# Revit family: Lighting-Recessed-Ledalite-TruGroove-LED_Flat_Corner V
name_source: partatom
category: Lighting Fixtures
revit_build: Autodesk Revit 2017 (Build: 20160720_1515(x64)
units: mm (PartAtom-declared; Revit-internal decimal feet)

## family parameters
Cut with Voids When Loaded = No
Host = Face
Light Source = Yes
OmniClass Number = 23.80.70.11.14
OmniClass Title = General Luminaries, Directional
Part Type = Normal
Room Calculation Point = No
Round Connector Dimension = Use Diameter
Shared = No

## types (135) — shared parameters
Assembly Code = D5020200
CIE Type = Direct
Color Filter = 16777215
Default Elevation = 48"
Dimming Lamp Color Temperature Shift = <None>
Fixture Efficiency = NA (Absolute Photometry)
Housing Length = 25 11/16"
Housing Material Finish = Paint-Signify-White
Housing Width = 3 7/16"
Lamp = LED
Last Updated = 11/6/2014
Lens Material Finish = Acrylic-Signify-White, Translucent
Lens Width = 3"
Manufacturer = Ledalite
NEMA Type = Not Applicable
Photometry Comments = Candela values are absolute.
Product Family = TruGroove
Product Page URL = http://www.lightingproducts.philips.com
Tilt Angle = -90.00°
URL = https://www.signify.com
Voltage = 120 V
eCatalog URL = www.ledalite.com

## per-type parameters (varying)
| type | Apparent Load | Depth | Depth below Ceiling | Description | LER Luminaire Efficacy Rating | Photometric Web File | Spacing to Mounting Height Ratio 0 Degree Plane | Spacing to Mounting Height Ratio 90 Degree Plane | Spacing to Mounting Height Ratio Diagonal | Trim | Trim Length | Trim Width | Trimless/TGrid |
| 39A0LAELx122 | 42 VA | 4 23/32" | 0" | 2x2 Flat Corner, Definition LED, 4000K, 3000 Nominal Delivered Lumens, Flush Silk Lens, T-Grid | 72 | 39x0LAELxx04.ies | 1.28 | 1.28 | 1.4 | No | 25 29/32" | 4" | Yes |
| 39A0LAELx422 | 42 VA | 4 7/8" | 5/32" | 2x2 Flat Corner, Definition LED, 4000K, 3000 Nominal Delivered Lumens, Flush Silk Lens, Drywall Trim | 72 | 39x0LAELxx04.ies | 1.28 | 1.28 | 1.4 | Yes | 26 5/16" | 4 1/2" | No |
| 39A0LAELx322 | 42 VA | 4 7/8" | 5/32" | 2x2 Flat Corner, Definition LED, 4000K, 3000 Nominal Delivered Lumens, Flush Silk Lens, Drywall Trimless | 72 | 39x0LAELxx04.ies | 1.28 | 1.28 | 1.4 | No | 27 3/32" | 6 1/4" | Yes |
| 39A0LAEMx122 | 42 VA | 4 23/32" | 0" | 2x2 Flat Corner, Definition LED, 4000K, 3000 Nominal Delivered Lumens, Regressed Silk Lens, T-Grid | 60 | 39x0LAEMxx04.ies | 1.28 | 1.24 | 1.36 | No | 25 29/32" | 4" | Yes |
| 39A0LAEMx422 | 42 VA | 4 7/8" | 5/32" | 2x2 Flat Corner, Definition LED, 4000K, 3000 Nominal Delivered Lumens, Regressed Silk Lens, Drywall Trim | 60 | 39x0LAEMxx04.ies | 1.28 | 1.24 | 1.36 | Yes | 26 5/16" | 4 1/2" | No |
| 39A0LAEMx322 | 42 VA | 4 7/8" | 5/32" | 2x2 Flat Corner, Definition LED, 4000K, 3000 Nominal Delivered Lumens, Regressed Silk Lens, Drywall Trimless | 60 | 39x0LAEMxx04.ies | 1.28 | 1.24 | 1.36 | No | 27 3/32" | 6 1/4" | Yes |
| 39A0LAGLx122 | 28 VA | 4 23/32" | 0" | 2x2 Flat Corner, Definition LED, 4000K, 2200 Nominal Delivered Lumens, Flush Silk Lens, T-Grid | 77 | 39x0LAGLxx04.ies | 1.28 | 1.28 | 1.4 | No | 25 29/32" | 4" | Yes |
| 39A0LAGLx422 | 28 VA | 4 7/8" | 5/32" | 2x2 Flat Corner, Definition LED, 4000K, 2200 Nominal Delivered Lumens, Flush Silk Lens, Drywall Trim | 77 | 39x0LAGLxx04.ies | 1.28 | 1.28 | 1.4 | Yes | 26 5/16" | 4 1/2" | No |
| 39A0LAGLx322 | 28 VA | 4 7/8" | 5/32" | 2x2 Flat Corner, Definition LED, 4000K, 2200 Nominal Delivered Lumens, Flush Silk Lens, Drywall Trimless | 77 | 39x0LAGLxx04.ies | 1.28 | 1.28 | 1.4 | No | 27 3/32" | 6 1/4" | Yes |
| 39A0LAGMx122 | 28 VA | 4 23/32" | 0" | 2x2 Flat Corner, Definition LED, 4000K, 2200 Nominal Delivered Lumens, Regressed Silk Lens, T-Grid | 64 | 39x0LAGMxx04.ies | 1.28 | 1.24 | 1.36 | No | 25 29/32" | 4" | Yes |
| 39A0LAGMx422 | 28 VA | 4 7/8" | 5/32" | 2x2 Flat Corner, Definition LED, 4000K, 2200 Nominal Delivered Lumens, Regressed Silk Lens, Drywall Trim | 64 | 39x0LAGMxx04.ies | 1.28 | 1.24 | 1.36 | Yes | 26 5/16" | 4 1/2" | No |
| 39A0LAGMx322 | 28 VA | 4 7/8" | 5/32" | 2x2 Flat Corner, Definition LED, 4000K, 2200 Nominal Delivered Lumens, Regressed Silk Lens, Drywall Trimless | 64 | 39x0LAGMxx04.ies | 1.28 | 1.24 | 1.36 | No | 27 3/32" | 6 1/4" | Yes |
| 39A0LAKLx122 | 19 VA | 4 23/32" | 0" | 2x2 Flat Corner, Definition LED, 4000K, 1500 Nominal Delivered Lumens, Flush Silk Lens, T-Grid | 80 | 39x0LAKLxx04.ies | 1.28 | 1.28 | 1.4 | No | 25 29/32" | 4" | Yes |
| 39A0LAKLx422 | 19 VA | 4 7/8" | 5/32" | 2x2 Flat Corner, Definition LED, 4000K, 1500 Nominal Delivered Lumens, Flush Silk Lens, Drywall Trim | 80 | 39x0LAKLxx04.ies | 1.28 | 1.28 | 1.4 | Yes | 26 5/16" | 4 1/2" | No |
| 39A0LAKLx322 | 19 VA | 4 7/8" | 5/32" | 2x2 Flat Corner, Definition LED, 4000K, 1500 Nominal Delivered Lumens, Flush Silk Lens, Drywall Trimless | 80 | 39x0LAKLxx04.ies | 1.28 | 1.28 | 1.4 | No | 27 3/32" | 6 1/4" | Yes |
| 39A0LAKMx122 | 19 VA | 4 23/32" | 0" | 2x2 Flat Corner, Definition LED, 4000K, 1500 Nominal Delivered Lumens, Regressed Silk Lens, T-Grid | 66 | 39x0LAKMxx04.ies | 1.28 | 1.24 | 1.36 | No | 25 29/32" | 4" | Yes |
| 39A0LAKMx422 | 19 VA | 4 7/8" | 5/32" | 2x2 Flat Corner, Definition LED, 4000K, 1500 Nominal Delivered Lumens, Regressed Silk Lens, Drywall Trim | 66 | 39x0LAKMxx04.ies | 1.28 | 1.24 | 1.36 | Yes | 26 5/16" | 4 1/2" | No |
| 39A0LAKMx322 | 19 VA | 4 7/8" | 5/32" | 2x2 Flat Corner, Definition LED, 4000K, 1500 Nominal Delivered Lumens, Regressed Silk Lens, Drywall Trimless | 66 | 39x0LAKMxx04.ies | 1.28 | 1.24 | 1.36 | No | 27 3/32" | 6 1/4" | Yes |
| 39A0LBELx122 | 41 VA | 4 23/32" | 0" | 2x2 Flat Corner, Definition LED, 3500K, 3000 Nominal Delivered Lumens, Flush Silk Lens, T-Grid | 73 | 39x0LBELxx04.ies | 1.28 | 1.28 | 1.4 | No | 25 29/32" | 4" | Yes |
| 39A0LBELx422 | 41 VA | 4 7/8" | 5/32" | 2x2 Flat Corner, Definition LED, 3500K, 3000 Nominal Delivered Lumens, Flush Silk Lens, Drywall Trim | 73 | 39x0LBELxx04.ies | 1.28 | 1.28 | 1.4 | Yes | 26 5/16" | 4 1/2" | No |
| 39A0LBELx322 | 41 VA | 4 7/8" | 5/32" | 2x2 Flat Corner, Definition LED, 3500K, 3000 Nominal Delivered Lumens, Flush Silk Lens, Drywall Trimless | 73 | 39x0LBELxx04.ies | 1.28 | 1.28 | 1.4 | No | 27 3/32" | 6 1/4" | Yes |
| 39A0LBEMx122 | 42 VA | 4 23/32" | 0" | 2x2 Flat Corner, Definition LED, 3500K, 3000 Nominal Delivered Lumens, Regressed Silk Lens, T-Grid | 61 | 39x0LBEMxx04.ies | 1.28 | 1.24 | 1.36 | No | 25 29/32" | 4" | Yes |
| 39A0LBEMx422 | 42 VA | 4 7/8" | 5/32" | 2x2 Flat Corner, Definition LED, 3500K, 3000 Nominal Delivered Lumens, Regressed Silk Lens, Drywall Trim | 61 | 39x0LBEMxx04.ies | 1.28 | 1.24 | 1.36 | Yes | 26 5/16" | 4 1/2" | No |
| 39A0LBEMx322 | 42 VA | 4 7/8" | 5/32" | 2x2 Flat Corner, Definition LED, 3500K, 3000 Nominal Delivered Lumens, Regressed Silk Lens, Drywall Trimless | 61 | 39x0LBEMxx04.ies | 1.28 | 1.24 | 1.36 | No | 27 3/32" | 6 1/4" | Yes |
| 39A0LBGLx122 | 28 VA | 4 23/32" | 0" | 2x2 Flat Corner, Definition LED, 3500K, 2200 Nominal Delivered Lumens, Flush Silk Lens, T-Grid | 78 | 39x0LBGLxx04.ies | 1.28 | 1.28 | 1.4 | No | 25 29/32" | 4" | Yes |
| 39A0LBGLx422 | 28 VA | 4 7/8" | 5/32" | 2x2 Flat Corner, Definition LED, 3500K, 2200 Nominal Delivered Lumens, Flush Silk Lens, Drywall Trim | 78 | 39x0LBGLxx04.ies | 1.28 | 1.28 | 1.4 | Yes | 26 5/16" | 4 1/2" | No |
| 39A0LBGLx322 | 28 VA | 4 7/8" | 5/32" | 2x2 Flat Corner, Definition LED, 3500K, 2200 Nominal Delivered Lumens, Flush Silk Lens, Drywall Trimless | 78 | 39x0LBGLxx04.ies | 1.28 | 1.28 | 1.4 | No | 27 3/32" | 6 1/4" | Yes |
| 39A0LBGMx122 | 28 VA | 4 23/32" | 0" | 2x2 Flat Corner, Definition LED, 3500K, 2200 Nominal Delivered Lumens, Regressed Silk Lens, T-Grid | 66 | 39x0LBGMxx04.ies | 1.28 | 1.24 | 1.36 | No | 25 29/32" | 4" | Yes |
| 39A0LBGMx422 | 28 VA | 4 7/8" | 5/32" | 2x2 Flat Corner, Definition LED, 3500K, 2200 Nominal Delivered Lumens, Regressed Silk Lens, Drywall Trim | 66 | 39x0LBGMxx04.ies | 1.28 | 1.24 | 1.36 | Yes | 26 5/16" | 4 1/2" | No |
| 39A0LBGMx322 | 28 VA | 4 7/8" | 5/32" | 2x2 Flat Corner, Definition LED, 3500K, 2200 Nominal Delivered Lumens, Regressed Silk Lens, Drywall Trimless | 66 | 39x0LBGMxx04.ies | 1.28 | 1.24 | 1.36 | No | 27 3/32" | 6 1/4" | Yes |
| 39A0LBKLx122 | 19 VA | 4 23/32" | 0" | 2x2 Flat Corner, Definition LED, 3500K, 1500 Nominal Delivered Lumens, Flush Silk Lens, T-Grid | 81 | 39x0LBKLxx04.ies | 1.28 | 1.28 | 1.4 | No | 25 29/32" | 4" | Yes |
| 39A0LBKLx422 | 19 VA | 4 7/8" | 5/32" | 2x2 Flat Corner, Definition LED, 3500K, 1500 Nominal Delivered Lumens, Flush Silk Lens, Drywall Trim | 81 | 39x0LBKLxx04.ies | 1.28 | 1.28 | 1.4 | Yes | 26 5/16" | 4 1/2" | No |
| 39A0LBKLx322 | 19 VA | 4 7/8" | 5/32" | 2x2 Flat Corner, Definition LED, 3500K, 1500 Nominal Delivered Lumens, Flush Silk Lens, Drywall Trimless | 81 | 39x0LBKLxx04.ies | 1.28 | 1.28 | 1.4 | No | 27 3/32" | 6 1/4" | Yes |
| 39A0LBKMx122 | 19 VA | 4 23/32" | 0" | 2x2 Flat Corner, Definition LED, 3500K, 1500 Nominal Delivered Lumens, Regressed Silk Lens, T-Grid | 67 | 39x0LBKMxx04.ies | 1.28 | 1.24 | 1.36 | No | 25 29/32" | 4" | Yes |
| 39A0LBKMx422 | 19 VA | 4 7/8" | 5/32" | 2x2 Flat Corner, Definition LED, 3500K, 1500 Nominal Delivered Lumens, Regressed Silk Lens, Drywall Trim | 67 | 39x0LBKMxx04.ies | 1.28 | 1.24 | 1.36 | Yes | 26 5/16" | 4 1/2" | No |
| 39A0LBKMx322 | 0 VA | 4 7/8" | 5/32" | 2x2 Flat Corner, Definition LED, 3500K, 1500 Nominal Delivered Lumens, Regressed Silk Lens, Drywall Trimless | 67 | 39x0LBKMxx04.ies | 1.28 | 1.24 | 1.36 | No | 27 3/32" | 6 1/4" | Yes |
| 39A0LCELx122 | 42 VA | 4 23/32" | 0" | 2x2 Flat Corner, Definition LED, 3000K, 3000 Nominal Delivered Lumens, Flush Silk Lens, T-Grid | 70 | 39x0LCELxx04.ies | 1.28 | 1.28 | 1.4 | No | 25 29/32" | 4" | Yes |
| 39A0LCELx422 | 42 VA | 4 7/8" | 5/32" | 2x2 Flat Corner, Definition LED, 3000K, 3000 Nominal Delivered Lumens, Flush Silk Lens, Drywall Trim | 70 | 39x0LCELxx04.ies | 1.28 | 1.28 | 1.4 | Yes | 26 5/16" | 4 1/2" | No |
| 39A0LCELx322 | 42 VA | 4 7/8" | 5/32" | 2x2 Flat Corner, Definition LED, 3000K, 3000 Nominal Delivered Lumens, Flush Silk Lens, Drywall Trimless | 70 | 39x0LCELxx04.ies | 1.28 | 1.28 | 1.4 | No | 27 3/32" | 6 1/4" | Yes |
| 39A0LCEMx122 | 42 VA | 4 23/32" | 0" | 2x2 Flat Corner, Definition LED, 3000K, 3000 Nominal Delivered Lumens, Regressed Silk Lens, T-Grid | 58 | 39x0LCEMxx04.ies | 1.28 | 1.24 | 1.36 | No | 25 29/32" | 4" | Yes |
| 39A0LCEMx422 | 42 VA | 4 7/8" | 5/32" | 2x2 Flat Corner, Definition LED, 3000K, 3000 Nominal Delivered Lumens, Regressed Silk Lens, Drywall Trim | 58 | 39x0LCEMxx04.ies | 1.28 | 1.24 | 1.36 | Yes | 26 5/16" | 4 1/2" | No |
| 39A0LCEMx322 | 42 VA | 4 7/8" | 5/32" | 2x2 Flat Corner, Definition LED, 3000K, 3000 Nominal Delivered Lumens, Regressed Silk Lens, Drywall Trimless | 58 | 39x0LCEMxx04.ies | 1.28 | 1.24 | 1.36 | No | 27 3/32" | 6 1/4" | Yes |
| 39A0LCGLx122 | 28 VA | 4 23/32" | 0" | 2x2 Flat Corner, Definition LED, 3000K, 2200 Nominal Delivered Lumens, Flush Silk Lens, T-Grid | 75 | 39x0LCGLxx04.ies | 1.28 | 1.28 | 1.4 | No | 25 29/32" | 4" | Yes |
| 39A0LCGLx422 | 28 VA | 4 7/8" | 5/32" | 2x2 Flat Corner, Definition LED, 3000K, 2200 Nominal Delivered Lumens, Flush Silk Lens, Drywall Trim | 75 | 39x0LCGLxx04.ies | 1.28 | 1.28 | 1.4 | Yes | 26 5/16" | 4 1/2" | No |
| 39A0LCGLx322 | 28 VA | 4 7/8" | 5/32" | 2x2 Flat Corner, Definition LED, 3000K, 2200 Nominal Delivered Lumens, Flush Silk Lens, Drywall Trimless | 75 | 39x0LCGLxx04.ies | 1.28 | 1.28 | 1.4 | No | 27 3/32" | 6 1/4" | Yes |
| 39A0LCGMx122 | 28 VA | 4 23/32" | 0" | 2x2 Flat Corner, Definition LED, 3000K, 2200 Nominal Delivered Lumens, Regressed Silk Lens, T-Grid | 62 | 39x0LCGMxx04.ies | 1.28 | 1.24 | 1.36 | No | 25 29/32" | 4" | Yes |
| 39A0LCGMx422 | 28 VA | 4 7/8" | 5/32" | 2x2 Flat Corner, Definition LED, 3000K, 2200 Nominal Delivered Lumens, Regressed Silk Lens, Drywall Trim | 62 | 39x0LCGMxx04.ies | 1.28 | 1.24 | 1.36 | Yes | 26 5/16" | 4 1/2" | No |
| 39A0LCGMx322 | 28 VA | 4 7/8" | 5/32" | 2x2 Flat Corner, Definition LED, 3000K, 2200 Nominal Delivered Lumens, Regressed Silk Lens, Drywall Trimless | 62 | 39x0LCGMxx04.ies | 1.28 | 1.24 | 1.36 | No | 27 3/32" | 6 1/4" | Yes |
| 39A0LCKLx122 | 19 VA | 4 23/32" | 0" | 2x2 Flat Corner, Definition LED, 3000K, 1500 Nominal Delivered Lumens, Flush Silk Lens, T-Grid | 77 | 39x0LCKLxx04.ies | 1.28 | 1.28 | 1.4 | No | 25 29/32" | 4" | Yes |
| 39A0LCKLx422 | 19 VA | 4 7/8" | 5/32" | 2x2 Flat Corner, Definition LED, 3000K, 1500 Nominal Delivered Lumens, Flush Silk Lens, Drywall Trim | 77 | 39x0LCKLxx04.ies | 1.28 | 1.28 | 1.4 | Yes | 26 5/16" | 4 1/2" | No |
| 39A0LCKLx322 | 19 VA | 4 7/8" | 5/32" | 2x2 Flat Corner, Definition LED, 3000K, 1500 Nominal Delivered Lumens, Flush Silk Lens, Drywall Trimless | 77 | 39x0LCKLxx04.ies | 1.28 | 1.28 | 1.4 | No | 27 3/32" | 6 1/4" | Yes |
| 39A0LCKMx122 | 19 VA | 4 23/32" | 0" | 2x2 Flat Corner, Definition LED, 3000K, 1500 Nominal Delivered Lumens, Regressed Silk Lens, T-Grid | 65 | 39x0LCKMxx04.ies | 1.28 | 1.24 | 1.36 | No | 25 29/32" | 4" | Yes |
| 39A0LCKMx422 | 19 VA | 4 7/8" | 5/32" | 2x2 Flat Corner, Definition LED, 3000K, 1500 Nominal Delivered Lumens, Regressed Silk Lens, Drywall Trim | 65 | 39x0LCKMxx04.ies | 1.28 | 1.24 | 1.36 | Yes | 26 5/16" | 4 1/2" | No |
| 39A0LCKMx322 | 19 VA | 4 7/8" | 5/32" | 2x2 Flat Corner, Definition LED, 3000K, 1500 Nominal Delivered Lumens, Regressed Silk Lens, Drywall Trimless | 65 | 39x0LCKMxx04.ies | 1.28 | 1.24 | 1.36 | No | 27 3/32" | 6 1/4" | Yes |
| 39A1LAEQx122 | 42 VA | 4 23/32" | 0" | 2x2 Flat Corner, Performance LED, 4000K, 3000 Nominal Delivered Lumens, Flush Meso Lens, T- Grid | 73 | 39x1LAEQxx04.ies | 1.42 | 1.76 | 1.52 | No | 25 29/32" | 4" | Yes |
| 39A1LAEQx422 | 42 VA | 4 7/8" | 5/32" | 2x2 Flat Corner, Performance LED, 4000K, 3000 Nominal Delivered Lumens, Flush Meso Lens, Drywall Trim | 73 | 39x1LAEQxx04.ies | 1.42 | 1.76 | 1.52 | Yes | 26 5/16" | 4 1/2" | No |
| 39A1LAEQx322 | 42 VA | 4 7/8" | 5/32" | 2x2 Flat Corner, Performance LED, 4000K, 3000 Nominal Delivered Lumens, Flush Meso Lens, Drywall Trimless | 73 | 39x1LAEQxx04.ies | 1.42 | 1.76 | 1.52 | No | 27 3/32" | 6 1/4" | Yes |
| 39A1LAERx122 | 42 VA | 4 23/32" | 0" | 2x2 Flat Corner, Performance LED, 4000K, 3000 Nominal Delivered Lumens, Regressed Meso Lens, T- Grid | 64 | 39x1LAERxx04.ies | 1.34 | 1.5 | 1.4 | No | 25 29/32" | 4" | Yes |
| 39A1LAERx422 | 42 VA | 4 7/8" | 5/32" | 2x2 Flat Corner, Performance LED, 4000K, 3000 Nominal Delivered Lumens, Regressed Meso Lens, Drywall Trim | 64 | 39x1LAERxx04.ies | 1.34 | 1.5 | 1.4 | Yes | 26 5/16" | 4 1/2" | No |
| 39A1LAERx322 | 42 VA | 4 7/8" | 5/32" | 2x2 Flat Corner, Performance LED, 4000K, 3000 Nominal Delivered Lumens, Regressed Meso Lens, Drywall Trimless | 64 | 39x1LAERxx04.ies | 1.34 | 1.5 | 1.4 | No | 27 3/32" | 6 1/4" | Yes |
| 39A1LAGQx122 | 28 VA | 4 23/32" | 0" | 2x2 Flat Corner, Performance LED, 4000K, 2200 Nominal Delivered Lumens, Flush Meso Lens, T- Grid | 78 | 39x1LAGQxx04.ies | 1.42 | 1.76 | 1.52 | No | 25 29/32" | 4" | Yes |
| 39A1LAGQx422 | 28 VA | 4 7/8" | 5/32" | 2x2 Flat Corner, Performance LED, 4000K, 2200 Nominal Delivered Lumens, Flush Meso Lens, Drywall Trim | 78 | 39x1LAGQxx04.ies | 1.42 | 1.76 | 1.52 | Yes | 26 5/16" | 4 1/2" | No |
| 39A1LAGQx322 | 28 VA | 4 7/8" | 5/32" | 2x2 Flat Corner, Performance LED, 4000K, 2200 Nominal Delivered Lumens, Flush Meso Lens, Drywall Trimless | 78 | 39x1LAGQxx04.ies | 1.42 | 1.76 | 1.52 | No | 27 3/32" | 6 1/4" | Yes |
| 39A1LAGRx122 | 28 VA | 4 23/32" | 0" | 2x2 Flat Corner, Performance LED, 4000K, 2200 Nominal Delivered Lumens, Regressed Meso Lens, T- Grid | 69 | 39x1LAGRxx04.ies | 1.34 | 1.5 | 1.4 | No | 25 29/32" | 4" | Yes |
| 39A1LAGRx422 | 28 VA | 4 7/8" | 5/32" | 2x2 Flat Corner, Performance LED, 4000K, 2200 Nominal Delivered Lumens, Regressed Meso Lens, Drywall Trim | 69 | 39x1LAGRxx04.ies | 1.34 | 1.5 | 1.4 | Yes | 26 5/16" | 4 1/2" | No |
| 39A1LAGRx322 | 28 VA | 4 7/8" | 5/32" | 2x2 Flat Corner, Performance LED, 4000K, 2200 Nominal Delivered Lumens, Regressed Meso Lens, Drywall Trimless | 69 | 39x1LAGRxx04.ies | 1.34 | 1.5 | 1.4 | No | 27 3/32" | 6 1/4" | Yes |
| 39A1LAKQx122 | 19 VA | 4 23/32" | 0" | 2x2 Flat Corner, Performance LED, 4000K, 1500 Nominal Delivered Lumens, Flush Meso Lens, T- Grid | 81 | 39x1LAKQxx04.ies | 1.42 | 1.76 | 1.52 | No | 25 29/32" | 4" | Yes |
| 39A1LAKQx422 | 19 VA | 4 7/8" | 5/32" | 2x2 Flat Corner, Performance LED, 4000K, 1500 Nominal Delivered Lumens, Flush Meso Lens, Drywall Trim | 81 | 39x1LAKQxx04.ies | 1.42 | 1.76 | 1.52 | Yes | 26 5/16" | 4 1/2" | No |
| 39A1LAKQx322 | 19 VA | 4 7/8" | 5/32" | 2x2 Flat Corner, Performance LED, 4000K, 1500 Nominal Delivered Lumens, Flush Meso Lens, Drywall Trimless | 81 | 39x1LAKQxx04.ies | 1.42 | 1.76 | 1.52 | No | 27 3/32" | 6 1/4" | Yes |
| 39A1LAKRx122 | 19 VA | 4 23/32" | 0" | 2x2 Flat Corner, Performance LED, 4000K, 1500 Nominal Delivered Lumens, Regressed Meso Lens, T- Grid | 71 | 39x1LAKRxx04.ies | 1.34 | 1.5 | 1.4 | No | 25 29/32" | 4" | Yes |
| 39A1LAKRx422 | 19 VA | 4 7/8" | 5/32" | 2x2 Flat Corner, Performance LED, 4000K, 1500 Nominal Delivered Lumens, Regressed Meso Lens, Drywall Trim | 71 | 39x1LAKRxx04.ies | 1.34 | 1.5 | 1.4 | Yes | 26 5/16" | 4 1/2" | No |
| 39A1LAKRx322 | 19 VA | 4 7/8" | 5/32" | 2x2 Flat Corner, Performance LED, 4000K, 1500 Nominal Delivered Lumens, Regressed Meso Lens, Drywall Trimless | 71 | 39x1LAKRxx04.ies | 1.34 | 1.5 | 1.4 | No | 27 3/32" | 6 1/4" | Yes |
| 39A1LBEQx122 | 41 VA | 4 23/32" | 0" | 2x2 Flat Corner, Performance LED, 3500K, 3000 Nominal Delivered Lumens, Flush Meso Lens, T- Grid | 74 | 39x1LBEQxx04.ies | 1.42 | 1.76 | 1.52 | No | 25 29/32" | 4" | Yes |
| 39A1LBEQx422 | 41 VA | 4 7/8" | 5/32" | 2x2 Flat Corner, Performance LED, 3500K, 3000 Nominal Delivered Lumens, Flush Meso Lens, Drywall Trim | 74 | 39x1LBEQxx04.ies | 1.42 | 1.76 | 1.52 | Yes | 26 5/16" | 4 1/2" | No |
| 39A1LBEQx322 | 41 VA | 4 7/8" | 5/32" | 2x2 Flat Corner, Performance LED, 3500K, 3000 Nominal Delivered Lumens, Flush Meso Lens, Drywall Trimless | 74 | 39x1LBEQxx04.ies | 1.42 | 1.76 | 1.52 | No | 27 3/32" | 6 1/4" | Yes |
| 39A1LBERx122 | 42 VA | 4 23/32" | 0" | 2x2 Flat Corner, Performance LED, 3500K, 3000 Nominal Delivered Lumens, Regressed Meso Lens, T- Grid | 65 | 39x1LBERxx04.ies | 1.34 | 1.5 | 1.4 | No | 25 29/32" | 4" | Yes |
| 39A1LBERx422 | 42 VA | 4 7/8" | 5/32" | 2x2 Flat Corner, Performance LED, 3500K, 3000 Nominal Delivered Lumens, Regressed Meso Lens, Drywall Trim | 65 | 39x1LBERxx04.ies | 1.34 | 1.5 | 1.4 | Yes | 26 5/16" | 4 1/2" | No |
| 39A1LBERx322 | 42 VA | 4 7/8" | 5/32" | 2x2 Flat Corner, Performance LED, 3500K, 3000 Nominal Delivered Lumens, Regressed Meso Lens, Drywall Trimless | 65 | 39x1LBERxx04.ies | 1.34 | 1.5 | 1.4 | No | 27 3/32" | 6 1/4" | Yes |
| 39A1LBGQx122 | 28 VA | 4 23/32" | 0" | 2x2 Flat Corner, Performance LED, 3500K, 2200 Nominal Delivered Lumens, Flush Meso Lens, T- Grid | 80 | 39x1LBGQxx04.ies | 1.42 | 1.76 | 1.52 | No | 25 29/32" | 4" | Yes |
| 39A1LBGQx422 | 28 VA | 4 7/8" | 5/32" | 2x2 Flat Corner, Performance LED, 3500K, 2200 Nominal Delivered Lumens, Flush Meso Lens, Drywall Trim | 80 | 39x1LBGQxx04.ies | 1.42 | 1.76 | 1.52 | Yes | 26 5/16" | 4 1/2" | No |
| 39A1LBGQx322 | 28 VA | 4 7/8" | 5/32" | 2x2 Flat Corner, Performance LED, 3500K, 2200 Nominal Delivered Lumens, Flush Meso Lens, Drywall Trimless | 80 | 39x1LBGQxx04.ies | 1.42 | 1.76 | 1.52 | No | 27 3/32" | 6 1/4" | Yes |
| 39A1LBGRx122 | 28 VA | 4 23/32" | 0" | 2x2 Flat Corner, Performance LED, 3500K, 2200 Nominal Delivered Lumens, Regressed Meso Lens, T- Grid | 70 | 39x1LBGRxx04.ies | 1.34 | 1.5 | 1.4 | No | 25 29/32" | 4" | Yes |
| 39A1LBGRx422 | 28 VA | 4 7/8" | 5/32" | 2x2 Flat Corner, Performance LED, 3500K, 2200 Nominal Delivered Lumens, Regressed Meso Lens, Drywall Trim | 70 | 39x1LBGRxx04.ies | 1.34 | 1.5 | 1.4 | Yes | 26 5/16" | 4 1/2" | No |
| 39A1LBGRx322 | 28 VA | 4 7/8" | 5/32" | 2x2 Flat Corner, Performance LED, 3500K, 2200 Nominal Delivered Lumens, Regressed Meso Lens, Drywall Trimless | 70 | 39x1LBGRxx04.ies | 1.34 | 1.5 | 1.4 | No | 27 3/32" | 6 1/4" | Yes |
| 39A1LBKQx122 | 19 VA | 4 23/32" | 0" | 2x2 Flat Corner, Performance LED, 3500K, 1500 Nominal Delivered Lumens, Flush Meso Lens, T- Grid | 82 | 39x1LBKQxx04.ies | 1.42 | 1.76 | 1.52 | No | 25 29/32" | 4" | Yes |
| 39A1LBKQx422 | 19 VA | 4 7/8" | 5/32" | 2x2 Flat Corner, Performance LED, 3500K, 1500 Nominal Delivered Lumens, Flush Meso Lens, Drywall Trim | 82 | 39x1LBKQxx04.ies | 1.42 | 1.76 | 1.52 | Yes | 26 5/16" | 4 1/2" | No |
| 39A1LBKQx322 | 19 VA | 4 7/8" | 5/32" | 2x2 Flat Corner, Performance LED, 3500K, 1500 Nominal Delivered Lumens, Flush Meso Lens, Drywall Trimless | 82 | 39x1LBKQxx04.ies | 1.42 | 1.76 | 1.52 | No | 27 3/32" | 6 1/4" | Yes |
| 39A1LBKRx122 | 19 VA | 4 23/32" | 0" | 2x2 Flat Corner, Performance LED, 3500K, 1500 Nominal Delivered Lumens, Regressed Meso Lens, T- Grid | 72 | 39x1LBKRxx04.ies | 1.34 | 1.5 | 1.4 | No | 25 29/32" | 4" | Yes |
| 39A1LBKRx422 | 19 VA | 4 7/8" | 5/32" | 2x2 Flat Corner, Performance LED, 3500K, 1500 Nominal Delivered Lumens, Regressed Meso Lens, Drywall Trim | 72 | 39x1LBKRxx04.ies | 1.34 | 1.5 | 1.4 | Yes | 26 5/16" | 4 1/2" | No |
| 39A1LBKRx322 | 19 VA | 4 7/8" | 5/32" | 2x2 Flat Corner, Performance LED, 3500K, 1500 Nominal Delivered Lumens, Regressed Meso Lens, Drywall Trimless | 72 | 39x1LBKRxx04.ies | 1.34 | 1.5 | 1.4 | No | 27 3/32" | 6 1/4" | Yes |
| 39A1LCEQx122 | 42 VA | 4 23/32" | 0" | 2x2 Flat Corner, Performance LED, 3000K, 3000 Nominal Delivered Lumens, Flush Meso Lens, T- Grid | 71 | 39x1LCEQxx04.ies | 1.42 | 1.76 | 1.52 | No | 25 29/32" | 4" | Yes |
| 39A1LCEQx422 | 42 VA | 4 7/8" | 5/32" | 2x2 Flat Corner, Performance LED, 3000K, 3000 Nominal Delivered Lumens, Flush Meso Lens, Drywall Trim | 71 | 39x1LCEQxx04.ies | 1.42 | 1.76 | 1.52 | Yes | 26 5/16" | 4 1/2" | No |
| 39A1LCEQx322 | 42 VA | 4 7/8" | 5/32" | 2x2 Flat Corner, Performance LED, 3000K, 3000 Nominal Delivered Lumens, Flush Meso Lens, Drywall Trimless | 71 | 39x1LCEQxx04.ies | 1.42 | 1.76 | 1.52 | No | 27 3/32" | 6 1/4" | Yes |
| 39A1LCERx122 | 42 VA | 4 23/32" | 0" | 2x2 Flat Corner, Performance LED, 3000K, 3000 Nominal Delivered Lumens, Regressed Meso Lens, T- Grid | 63 | 39x1LCERxx04.ies | 1.34 | 1.5 | 1.4 | No | 25 29/32" | 4" | Yes |
| 39A1LCERx422 | 42 VA | 4 7/8" | 5/32" | 2x2 Flat Corner, Performance LED, 3000K, 3000 Nominal Delivered Lumens, Regressed Meso Lens, Drywall Trim | 63 | 39x1LCERxx04.ies | 1.34 | 1.5 | 1.4 | Yes | 26 5/16" | 4 1/2" | No |
| 39A1LCERx322 | 42 VA | 4 7/8" | 5/32" | 2x2 Flat Corner, Performance LED, 3000K, 3000 Nominal Delivered Lumens, Regressed Meso Lens, Drywall Trimless | 63 | 39x1LCERxx04.ies | 1.34 | 1.5 | 1.4 | No | 27 3/32" | 6 1/4" | Yes |
| 39A1LCGQx122 | 28 VA | 4 23/32" | 0" | 2x2 Flat Corner, Performance LED, 3000K, 2200 Nominal Delivered Lumens, Flush Meso Lens, T- Grid | 76 | 39x1LCGQxx04.ies | 1.42 | 1.76 | 1.52 | No | 25 29/32" | 4" | Yes |
| 39A1LCGQx422 | 28 VA | 4 7/8" | 5/32" | 2x2 Flat Corner, Performance LED, 3000K, 2200 Nominal Delivered Lumens, Flush Meso Lens, Drywall Trim | 76 | 39x1LCGQxx04.ies | 1.42 | 1.76 | 1.52 | Yes | 26 5/16" | 4 1/2" | No |
| 39A1LCGQx322 | 28 VA | 4 7/8" | 5/32" | 2x2 Flat Corner, Performance LED, 3000K, 2200 Nominal Delivered Lumens, Flush Meso Lens, Drywall Trimless | 76 | 39x1LCGQxx04.ies | 1.42 | 1.76 | 1.52 | No | 27 3/32" | 6 1/4" | Yes |
| 39A1LCGRx122 | 28 VA | 4 23/32" | 0" | 2x2 Flat Corner, Performance LED, 3000K, 2200 Nominal Delivered Lumens, Regressed Meso Lens, T- Grid | 67 | 39x1LCGRxx04.ies | 1.34 | 1.5 | 1.4 | No | 25 29/32" | 4" | Yes |
| 39A1LCGRx422 | 28 VA | 4 7/8" | 5/32" | 2x2 Flat Corner, Performance LED, 3000K, 2200 Nominal Delivered Lumens, Regressed Meso Lens, Drywall Trim | 67 | 39x1LCGRxx04.ies | 1.34 | 1.5 | 1.4 | Yes | 26 5/16" | 4 1/2" | No |
| 39A1LCGRx322 | 28 VA | 4 7/8" | 5/32" | 2x2 Flat Corner, Performance LED, 3000K, 2200 Nominal Delivered Lumens, Regressed Meso Lens, Drywall Trimless | 67 | 39x1LCGRxx04.ies | 1.34 | 1.5 | 1.4 | No | 27 3/32" | 6 1/4" | Yes |
| 39A1LCKQx122 | 19 VA | 4 23/32" | 0" | 2x2 Flat Corner, Performance LED, 3000K, 1500 Nominal Delivered Lumens, Flush Meso Lens, T- Grid | 78 | 39x1LCKQxx04.ies | 1.42 | 1.76 | 1.52 | No | 25 29/32" | 4" | Yes |
| 39A1LCKQx422 | 19 VA | 4 7/8" | 5/32" | 2x2 Flat Corner, Performance LED, 3000K, 1500 Nominal Delivered Lumens, Flush Meso Lens, Drywall Trim | 78 | 39x1LCKQxx04.ies | 1.42 | 1.76 | 1.52 | Yes | 26 5/16" | 4 1/2" | No |
| 39A1LCKQx322 | 19 VA | 4 7/8" | 5/32" | 2x2 Flat Corner, Performance LED, 3000K, 1500 Nominal Delivered Lumens, Flush Meso Lens, Drywall Trimless | 78 | 39x1LCKQxx04.ies | 1.42 | 1.76 | 1.52 | No | 27 3/32" | 6 1/4" | Yes |
| 39A1LCKRx122 | 19 VA | 4 23/32" | 0" | 2x2 Flat Corner, Performance LED, 3000K, 1500 Nominal Delivered Lumens, Regressed Meso Lens, T- Grid | 69 | 39x1LCKRxx04.ies | 1.34 | 1.5 | 1.4 | No | 25 29/32" | 4" | Yes |
| 39A1LCKRx422 | 19 VA | 4 7/8" | 5/32" | 2x2 Flat Corner, Performance LED, 3000K, 1500 Nominal Delivered Lumens, Regressed Meso Lens, Drywall Trim | 69 | 39x1LCKRxx04.ies | 1.34 | 1.5 | 1.4 | Yes | 26 5/16" | 4 1/2" | No |
| 39A1LCKRx322 | 19 VA | 4 7/8" | 5/32" | 2x2 Flat Corner, Performance LED, 3000K, 1500 Nominal Delivered Lumens, Regressed Meso Lens, Drywall Trimless | 69 | 39x1LCKRxx04.ies | 1.34 | 1.5 | 1.4 | No | 27 3/32" | 6 1/4" | Yes |
| 39A8LAEQx122 | 42 VA | 4 23/32" | 0" | 2x2 Flat Corner, Asymmetric LED, 4000K, 3000 Nominal Delivered Lumens, Flush Meso Lens, T-Grid | 71 | 39x8LAEQxx04.ies | 1.44 | 1.24 | 1.22 | No | 25 29/32" | 4" | Yes |
| 39A8LAEQx422 | 42 VA | 4 7/8" | 5/32" | 2x2 Flat Corner, Asymmetric LED, 4000K, 3000 Nominal Delivered Lumens, Flush Meso Lens, Drywall Trim | 71 | 39x8LAEQxx04.ies | 1.44 | 1.24 | 1.22 | Yes | 26 5/16" | 4 1/2" | No |
| 39A8LAEQx322 | 42 VA | 4 7/8" | 5/32" | 2x2 Flat Corner, Asymmetric LED, 4000K, 3000 Nominal Delivered Lumens, Flush Meso Lens, Drywall Trimless | 71 | 39x8LAEQxx04.ies | 1.44 | 1.24 | 1.22 | No | 27 3/32" | 6 1/4" | Yes |
| 39A8LAGQx122 | 28 VA | 4 23/32" | 0" | 2x2 Flat Corner, Asymmetric LED, 4000K, 2200 Nominal Delivered Lumens, Flush Meso Lens, T-Grid | 77 | 39x8LAGQxx04.ies | 1.44 | 1.24 | 1.22 | No | 25 29/32" | 4" | Yes |
| 39A8LAGQx422 | 28 VA | 4 7/8" | 5/32" | 2x2 Flat Corner, Asymmetric LED, 4000K, 2200 Nominal Delivered Lumens, Flush Meso Lens, Drywall Trim | 77 | 39x8LAGQxx04.ies | 1.44 | 1.24 | 1.22 | Yes | 26 5/16" | 4 1/2" | No |
| 39A8LAGQx322 | 0 VA | 4 7/8" | 5/32" | 2x2 Flat Corner, Asymmetric LED, 4000K, 2200 Nominal Delivered Lumens, Flush Meso Lens, Drywall Trimless | 77 | 39x8LAGQxx04.ies | 1.44 | 1.24 | 1.22 | No | 27 3/32" | 6 1/4" | Yes |
| 39A8LAKQx122 | 19 VA | 4 23/32" | 0" | 2x2 Flat Corner, Asymmetric LED, 4000K, 1500 Nominal Delivered Lumens, Flush Meso Lens, T-Grid | 79 | 39x8LAKQxx04.ies | 1.44 | 1.24 | 1.22 | No | 25 29/32" | 4" | Yes |
| 39A8LAKQx422 | 19 VA | 4 7/8" | 5/32" | 2x2 Flat Corner, Asymmetric LED, 4000K, 1500 Nominal Delivered Lumens, Flush Meso Lens, Drywall Trim | 79 | 39x8LAKQxx04.ies | 1.44 | 1.24 | 1.22 | Yes | 26 5/16" | 4 1/2" | No |
| 39A8LAKQx322 | 19 VA | 4 7/8" | 5/32" | 2x2 Flat Corner, Asymmetric LED, 4000K, 1500 Nominal Delivered Lumens, Flush Meso Lens, Drywall Trimless | 79 | 39x8LAKQxx04.ies | 1.44 | 1.24 | 1.22 | No | 27 3/32" | 6 1/4" | Yes |
| 39A8LBEQx122 | 42 VA | 4 23/32" | 0" | 2x2 Flat Corner, Asymmetric LED, 3500K, 3000 Nominal Delivered Lumens, Flush Meso Lens, T-Grid | 72 | 39x8LBEQxx04.ies | 1.44 | 1.24 | 1.22 | No | 25 29/32" | 4" | Yes |
| 39A8LBEQx422 | 42 VA | 4 7/8" | 5/32" | 2x2 Flat Corner, Asymmetric LED, 3500K, 3000 Nominal Delivered Lumens, Flush Meso Lens, Drywall Trim | 72 | 39x8LBEQxx04.ies | 1.44 | 1.24 | 1.22 | Yes | 26 5/16" | 4 1/2" | No |
| 39A8LBEQx322 | 42 VA | 4 7/8" | 5/32" | 2x2 Flat Corner, Asymmetric LED, 3500K, 3000 Nominal Delivered Lumens, Flush Meso Lens, Drywall Trimless | 72 | 39x8LBEQxx04.ies | 1.44 | 1.24 | 1.22 | No | 27 3/32" | 6 1/4" | Yes |
| 39A8LBGQx122 | 28 VA | 4 23/32" | 0" | 2x2 Flat Corner, Asymmetric LED, 3500K, 2200 Nominal Delivered Lumens, Flush Meso Lens, T-Grid | 78 | 39x8LBGQxx04.ies | 1.44 | 1.24 | 1.22 | No | 25 29/32" | 4" | Yes |
| 39A8LBGQx422 | 28 VA | 4 7/8" | 5/32" | 2x2 Flat Corner, Asymmetric LED, 3500K, 2200 Nominal Delivered Lumens, Flush Meso Lens, Drywall Trim | 78 | 39x8LBGQxx04.ies | 1.44 | 1.24 | 1.22 | Yes | 26 5/16" | 4 1/2" | No |
| 39A8LBGQx322 | 28 VA | 4 7/8" | 5/32" | 2x2 Flat Corner, Asymmetric LED, 3500K, 2200 Nominal Delivered Lumens, Flush Meso Lens, Drywall Trimless | 78 | 39x8LBGQxx04.ies | 1.44 | 1.24 | 1.22 | No | 27 3/32" | 6 1/4" | Yes |
| 39A8LBKQx122 | 19 VA | 4 23/32" | 0" | 2x2 Flat Corner, Asymmetric LED, 3500K, 1500 Nominal Delivered Lumens, Flush Meso Lens, T-Grid | 80 | 39x8LBKQxx04.ies | 1.44 | 1.24 | 1.22 | No | 25 29/32" | 4" | Yes |
| 39A8LBKQx422 | 19 VA | 4 7/8" | 5/32" | 2x2 Flat Corner, Asymmetric LED, 3500K, 1500 Nominal Delivered Lumens, Flush Meso Lens, Drywall Trim | 80 | 39x8LBKQxx04.ies | 1.44 | 1.24 | 1.22 | Yes | 26 5/16" | 4 1/2" | No |
| 39A8LBKQx322 | 19 VA | 4 7/8" | 5/32" | 2x2 Flat Corner, Asymmetric LED, 3500K, 1500 Nominal Delivered Lumens, Flush Meso Lens, Drywall Trimless | 80 | 39x8LBKQxx04.ies | 1.44 | 1.24 | 1.22 | No | 27 3/32" | 6 1/4" | Yes |
| 39A8LCEQx122 | 42 VA | 4 23/32" | 0" | 2x2 Flat Corner, Asymmetric LED, 3000K, 3000 Nominal Delivered Lumens, Flush Meso Lens, T-Grid | 69 | 39x8LCEQxx04.ies | 1.44 | 1.24 | 1.22 | No | 25 29/32" | 4" | Yes |
| 39A8LCEQx422 | 42 VA | 4 7/8" | 5/32" | 2x2 Flat Corner, Asymmetric LED, 3000K, 3000 Nominal Delivered Lumens, Flush Meso Lens, Drywall Trim | 69 | 39x8LCEQxx04.ies | 1.44 | 1.24 | 1.22 | Yes | 26 5/16" | 4 1/2" | No |
| 39A8LCEQx322 | 0 VA | 4 7/8" | 5/32" | 2x2 Flat Corner, Asymmetric LED, 3000K, 3000 Nominal Delivered Lumens, Flush Meso Lens, Drywall Trimless | 69 | 39x8LCEQxx04.ies | 1.44 | 1.24 | 1.22 | No | 27 3/32" | 6 1/4" | Yes |
| 39A8LCGQx122 | 28 VA | 4 23/32" | 0" | 2x2 Flat Corner, Asymmetric LED, 3000K, 2200 Nominal Delivered Lumens, Flush Meso Lens, T-Grid | 74 | 39x8LCGQxx04.ies | 1.44 | 1.24 | 1.22 | No | 25 29/32" | 4" | Yes |
| 39A8LCGQx422 | 28 VA | 4 7/8" | 5/32" | 2x2 Flat Corner, Asymmetric LED, 3000K, 2200 Nominal Delivered Lumens, Flush Meso Lens, Drywall Trim | 74 | 39x8LCGQxx04.ies | 1.44 | 1.24 | 1.22 | Yes | 26 5/16" | 4 1/2" | No |
| 39A8LCGQx322 | 28 VA | 4 7/8" | 5/32" | 2x2 Flat Corner, Asymmetric LED, 3000K, 2200 Nominal Delivered Lumens, Flush Meso Lens, Drywall Trimless | 74 | 39x8LCGQxx04.ies | 1.44 | 1.24 | 1.22 | No | 27 3/32" | 6 1/4" | Yes |
| 39A8LCKQx122 | 19 VA | 4 23/32" | 0" | 2x2 Flat Corner, Asymmetric LED, 3000K, 1500 Nominal Delivered Lumens, Flush Meso Lens, T-Grid | 77 | 39x8LCKQxx04.ies | 1.44 | 1.24 | 1.22 | No | 25 29/32" | 4" | Yes |
| 39A8LCKQx422 | 19 VA | 4 7/8" | 5/32" | 2x2 Flat Corner, Asymmetric LED, 3000K, 1500 Nominal Delivered Lumens, Flush Meso Lens, Drywall Trim | 77 | 39x8LCKQxx04.ies | 1.44 | 1.24 | 1.22 | Yes | 26 5/16" | 4 1/2" | No |
| 39A8LCKQx322 | 19 VA | 4 7/8" | 5/32" | 2x2 Flat Corner, Asymmetric LED, 3000K, 1500 Nominal Delivered Lumens, Flush Meso Lens, Drywall Trimless | 77 | 39x8LCKQxx04.ies | 1.44 | 1.24 | 1.22 | No | 27 3/32" | 6 1/4" | Yes |

note: column(s) folded — value = type name in every type: Catalog Number, Model

## geometry (parser evidence)
native form markers: Sweep x1
no freeform markers — native parametric forms only
